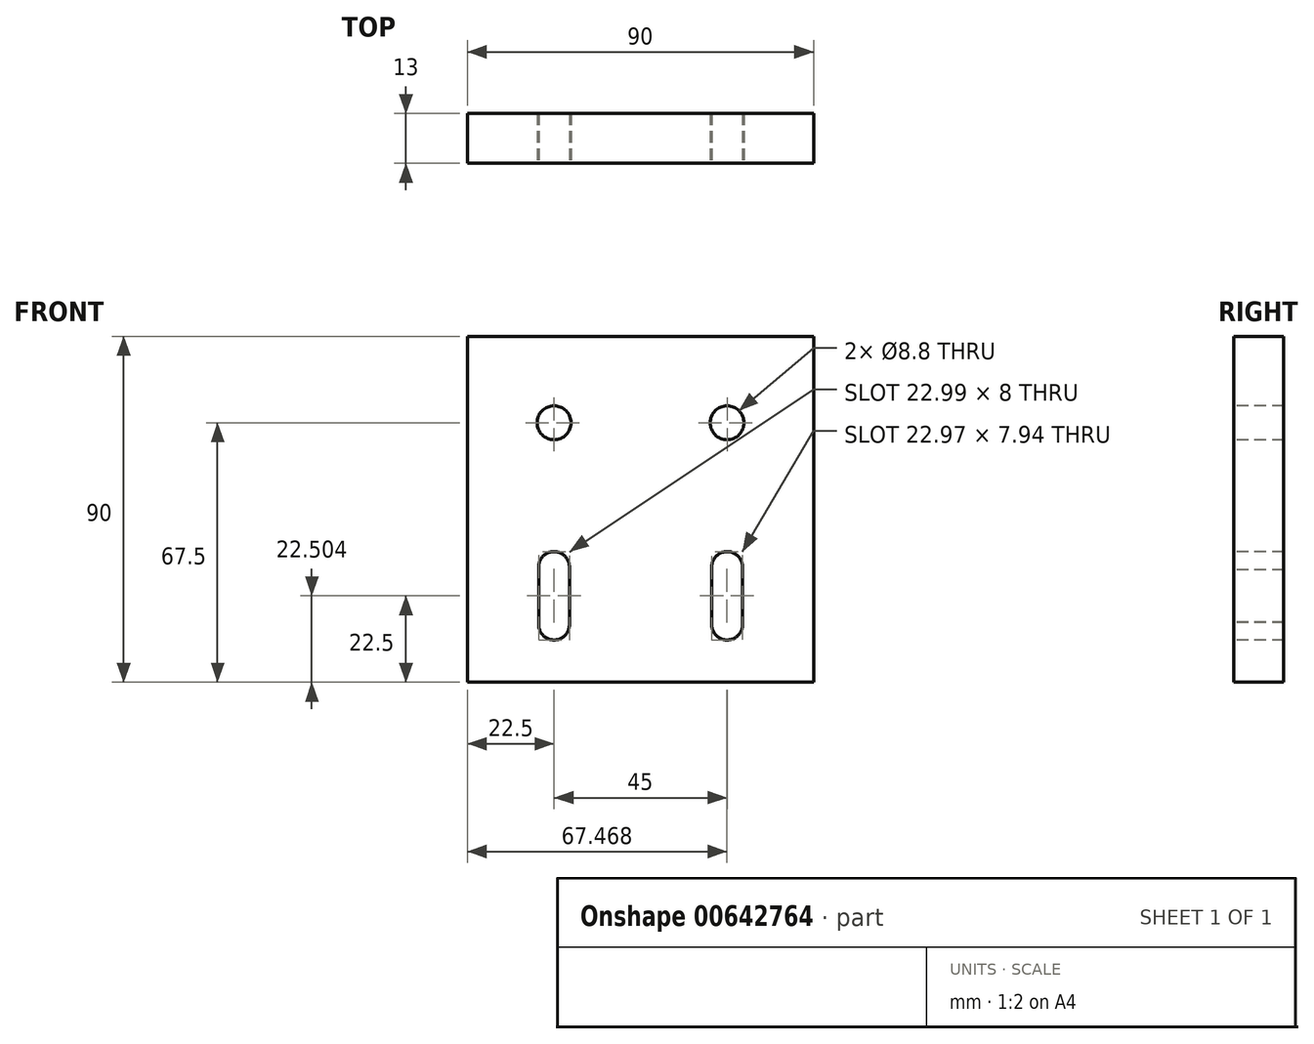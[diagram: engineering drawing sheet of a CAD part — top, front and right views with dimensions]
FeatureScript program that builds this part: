
annotation { "Feature Type Name" : "Feature", "Feature Type Description" : "" }
export const myFeature = defineFeature(function(context is Context, id is Id, definition is map)
    precondition{}
    {
        {
            var Q0;
            Q0=qCreatedBy(makeId("Front.planeOp"),FACE);
            var sketch = newSketch(context, id + "F0", { "sketchPlane" : qUnion([Q0])});
            skLineSegment(sketch, "E0.bottom", {"start": v(0, 0) * mm, "end": v(90, 0) * mm});
            skLineSegment(sketch, "E0.top", {"start": v(0, -90) * mm, "end": v(90, -90) * mm});
            skLineSegment(sketch, "E0.left", {"start": v(0, 0) * mm, "end": v(0, -90) * mm});
            skLineSegment(sketch, "E0.right", {"start": v(90, 0) * mm, "end": v(90, -90) * mm});
            skSolve(sketch);
        }
        {
            var Q0;
            Q0=makeQuery(id+"F0.imprint","IMPRINT",FACE,{"disambiguationData":[TD([[makeQuery(id+"F0.imprint","IMPRINT",EDGE,{"derivedFrom":sQuery(id+"F0.wireOp",EDGE,"E0.bottom")}),-1.0]])]});
            extrude(context, id + "F1", {"entities" : qUnion([Q0]), "depth" : 13 * mm, "offsetDistance" : 25 * mm});
        }
        {
            var Q0;
            Q0=makeQuery(id+"F1.opExtrude","CAP_FACE",FACE,{"disambiguationData":[OSD([sQuery(id+"F0.wireOp",EDGE,"E0.bottom"),sQuery(id+"F0.wireOp",EDGE,"E0.top"),sQuery(id+"F0.wireOp",EDGE,"E0.left"),sQuery(id+"F0.wireOp",EDGE,"E0.right")])],"isStart":false});
            var sketch = newSketch(context, id + "F2", { "sketchPlane" : qUnion([Q0])});
            skPoint(sketch, "E1", {"position": v(22.5, -22.5) * mm});
            skPoint(sketch, "E2", {"position": v(67.5, -22.5) * mm});
            skPoint(sketch, "E3", {"position": v(22.5, -60) * mm});
            skPoint(sketch, "E4", {"position": v(67.5, -60) * mm});
            skPoint(sketch, "E5", {"position": v(67.5, -75) * mm});
            skPoint(sketch, "E6", {"position": v(22.5, -75) * mm});
            skArc(sketch, "E7", {"start": v(71.44, -60.7) * mm, "mid": v(67.86, -56.02) * mm, "end": v(63.5, -60) * mm});
            skArc(sketch, "E8", {"start": v(26.5, -60) * mm, "mid": v(22.5, -56) * mm, "end": v(18.5, -60) * mm});
            skArc(sketch, "E9", {"start": v(63.5, -75) * mm, "mid": v(67.86, -78.98) * mm, "end": v(71.44, -74.3) * mm});
            skArc(sketch, "E10", {"start": v(18.53, -74.5) * mm, "mid": v(22.25, -79) * mm, "end": v(26.5, -75) * mm});
            skLineSegment(sketch, "E11", {"start": v(26.5, -75) * mm, "end": v(26.5, -60) * mm});
            skLineSegment(sketch, "E12", {"start": v(18.53, -74.5) * mm, "end": v(18.5, -60) * mm});
            skLineSegment(sketch, "E13", {"start": v(63.5, -75) * mm, "end": v(63.5, -60) * mm});
            skLineSegment(sketch, "E14", {"start": v(71.44, -59.3) * mm, "end": v(71.44, -74.3) * mm});
            skSolve(sketch);
        }
        {
            var Q0;
            Q0 = qSketchRegion(id + "F2", true);
            extrude(context, id + "F3", {"entities" : qUnion([Q0]), "operationType" : NewBodyOperationType.REMOVE, "oppositeDirection" : true, "depth" : 25 * mm, "offsetDistance" : 25 * mm});
        }
        {
            var Q0;
            Q0=sQuery(id+"F2.wireOp",VERTEX,"E1");
            var Q1;
            Q1=sQuery(id+"F2.wireOp",VERTEX,"E2");
            var Q2;
            Q2=makeQuery(id+"F1.opExtrude","SWEPT_BODY",BODY,{"disambiguationData":[OSD([sQuery(id+"F0.wireOp",EDGE,"E0.bottom"),sQuery(id+"F0.wireOp",EDGE,"E0.top"),sQuery(id+"F0.wireOp",EDGE,"E0.left"),sQuery(id+"F0.wireOp",EDGE,"E0.right")])]});
            hole(context, id + "F4", {"style" : HoleStyle.SIMPLE, "endStyle" : HoleEndStyle.BLIND, "standardTappedOrClearance" : lookupTablePath({ "standard" : "ISO", "fit" : "Normal", "size" : "M8", "type" : "Clearance" }), "standardBlindInLast" : lookupTablePath({ "fit" : "Standard", "standard" : "ISO", "size" : "M8", "type" : "Clearance" }), "holeDiameter" : 8.8 * mm, "majorDiameter" : 8 * mm, "holeDepth" : 18.25 * mm, "isTappedThrough" : true, "tappedDepth" : 14.5 * mm, "tapClearance" : 3, "startFromSketch" : true, "locations" : qUnion([Q0, Q1]), "scope" : qUnion([Q2])});
        }
    });
